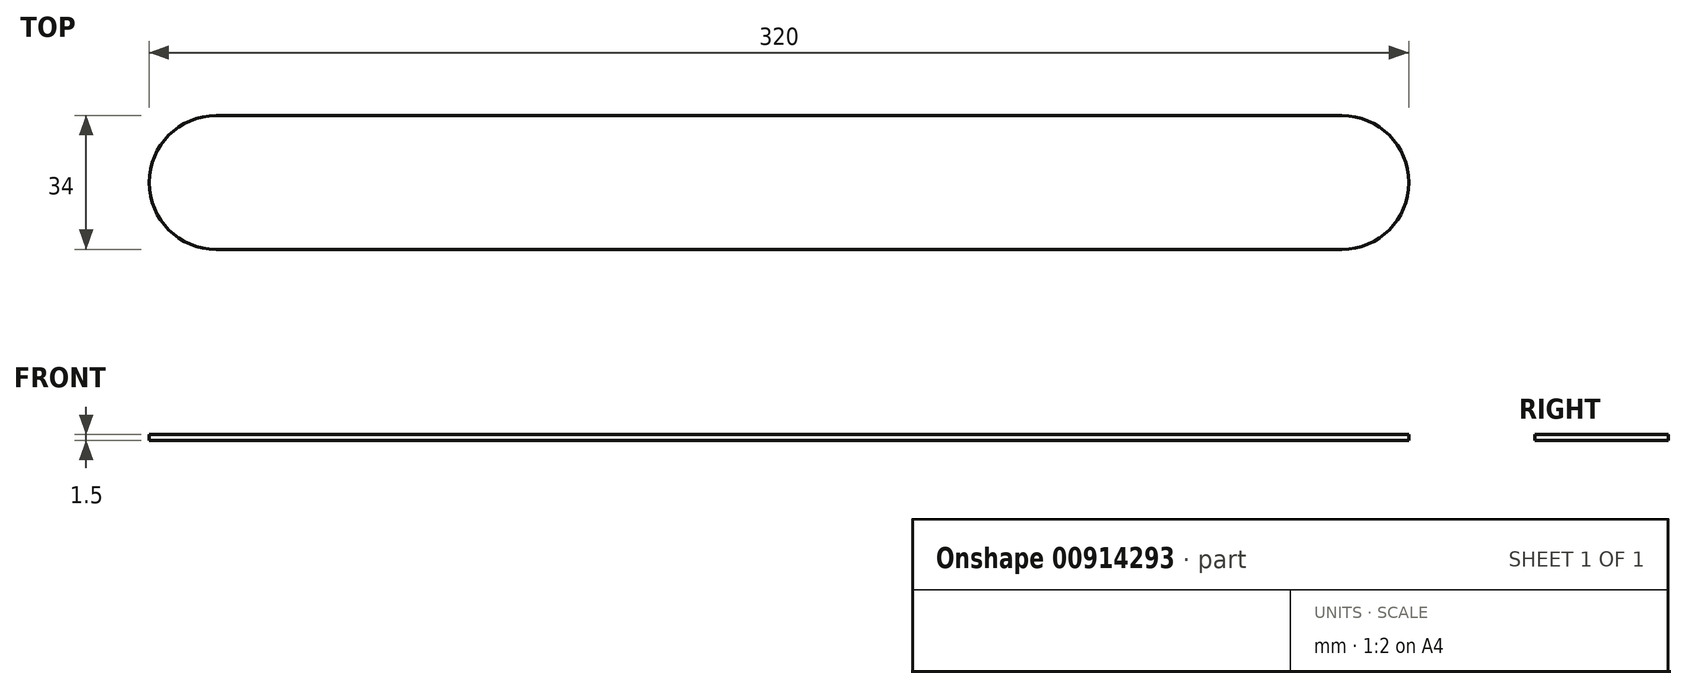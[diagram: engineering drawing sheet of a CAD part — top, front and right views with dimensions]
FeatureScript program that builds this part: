
annotation { "Feature Type Name" : "Feature", "Feature Type Description" : "" }
export const myFeature = defineFeature(function(context is Context, id is Id, definition is map)
    precondition{}
    {
        {
            var Q0;
            Q0=qCreatedBy(makeId("Top.planeOp"),FACE);
            var sketch = newSketch(context, id + "F0", { "sketchPlane" : qUnion([Q0])});
            skLineSegment(sketch, "E0", {"start": v(-143, 17) * mm, "end": v(143, 17) * mm});
            skLineSegment(sketch, "E1", {"start": v(-143, -17) * mm, "end": v(143, -17) * mm});
            skArc(sketch, "E2", {"start": v(-143, 17) * mm, "mid": v(-160, 0) * mm, "end": v(-143, -17) * mm});
            skArc(sketch, "E3", {"start": v(143, 17) * mm, "mid": v(160, 0) * mm, "end": v(143, -17) * mm});
            skPoint(sketch, "E4", {"position": v(-160, 0) * mm});
            skPoint(sketch, "E5", {"position": v(160, 0) * mm});
            skLineSegment(sketch, "E6", {"start": v(-160, 0) * mm, "end": v(160, 0) * mm, "construction": true});
            skSolve(sketch);
        }
        {
            var Q0;
            Q0 = qSketchRegion(id + "F0", true);
            extrude(context, id + "F1", {"entities" : qUnion([Q0]), "depth" : 1.5 * mm, "offsetDistance" : 25 * mm});
        }
    });
